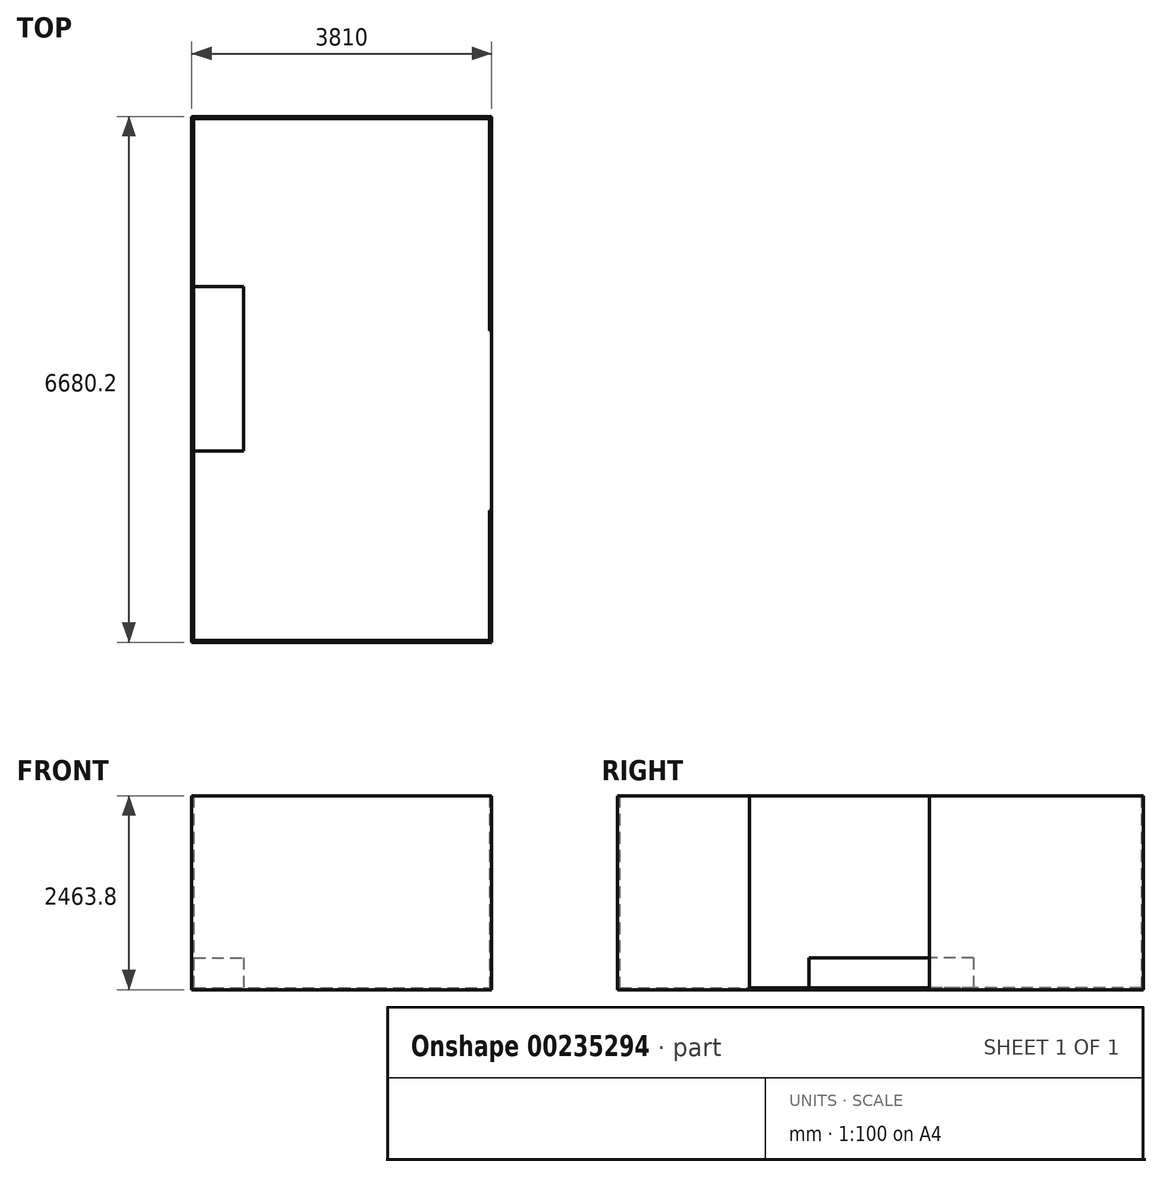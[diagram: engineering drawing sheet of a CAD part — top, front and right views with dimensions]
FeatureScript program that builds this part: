
annotation { "Feature Type Name" : "Feature", "Feature Type Description" : "" }
export const myFeature = defineFeature(function(context is Context, id is Id, definition is map)
    precondition{}
    {
        {
            var Q0;
            Q0=qCreatedBy(makeId("Top.planeOp"),FACE);
            var sketch = newSketch(context, id + "F0", { "sketchPlane" : qUnion([Q0])});
            skLineSegment(sketch, "E0", {"start": v(-1905, 3340.1) * mm, "end": v(1905, 3340.1) * mm});
            skLineSegment(sketch, "E1", {"start": v(1905, 3340.1) * mm, "end": v(1905, 622.3) * mm});
            skLineSegment(sketch, "E2", {"start": v(-1905, 3340.1) * mm, "end": v(-1905, -3340.1) * mm});
            skLineSegment(sketch, "E3", {"start": v(-1905, -3340.1) * mm, "end": v(1905, -3340.1) * mm});
            skLineSegment(sketch, "E4", {"start": v(1905, -3340.1) * mm, "end": v(1905, -1663.7) * mm});
            skLineSegment(sketch, "E5", {"start": v(0, 3340.1) * mm, "end": v(0, -3340.1) * mm, "construction": true});
            skLineSegment(sketch, "E6.0", {"start": v(1879.6, 3314.7) * mm, "end": v(1879.6, 622.3) * mm});
            skLineSegment(sketch, "E6.1", {"start": v(1879.6, -3314.7) * mm, "end": v(1879.6, -1663.7) * mm});
            skLineSegment(sketch, "E6.2", {"start": v(-1879.6, -3314.7) * mm, "end": v(1879.6, -3314.7) * mm});
            skLineSegment(sketch, "E6.3", {"start": v(-1879.6, 3314.7) * mm, "end": v(-1879.6, -3314.7) * mm});
            skLineSegment(sketch, "E6.4", {"start": v(-1879.6, 3314.7) * mm, "end": v(1879.6, 3314.7) * mm});
            skLineSegment(sketch, "E7", {"start": v(1879.6, -1663.7) * mm, "end": v(1905, -1663.7) * mm});
            skLineSegment(sketch, "E8", {"start": v(1879.6, 622.3) * mm, "end": v(1905, 622.3) * mm});
            skSolve(sketch);
        }
        {
            var Q0;
            Q0 = qSketchRegion(id + "F0", true);
            extrude(context, id + "F1", {"entities" : qUnion([Q0]), "depth" : 2438.4 * mm});
        }
        {
            var Q0;
            Q0=makeQuery(id+"F1.opExtrude","CAP_FACE",FACE,{"disambiguationData":[OSD([sQuery(id+"F0.wireOp",EDGE,"E0"),sQuery(id+"F0.wireOp",EDGE,"E1"),sQuery(id+"F0.wireOp",EDGE,"E2"),sQuery(id+"F0.wireOp",EDGE,"E3"),sQuery(id+"F0.wireOp",EDGE,"E4"),sQuery(id+"F0.wireOp",EDGE,"E6.0"),sQuery(id+"F0.wireOp",EDGE,"E6.1"),sQuery(id+"F0.wireOp",EDGE,"E6.2"),sQuery(id+"F0.wireOp",EDGE,"E6.3"),sQuery(id+"F0.wireOp",EDGE,"E6.4"),sQuery(id+"F0.wireOp",EDGE,"E7"),sQuery(id+"F0.wireOp",EDGE,"E8")])],"isStart":true});
            var sketch = newSketch(context, id + "F2", { "sketchPlane" : qUnion([Q0])});
            skLineSegment(sketch, "E9.bottom", {"start": v(-1905, 3340.1) * mm, "end": v(1905, 3340.1) * mm});
            skLineSegment(sketch, "E9.top", {"start": v(-1905, -3340.1) * mm, "end": v(1905, -3340.1) * mm});
            skLineSegment(sketch, "E9.left", {"start": v(-1905, 3340.1) * mm, "end": v(-1905, -3340.1) * mm});
            skLineSegment(sketch, "E9.right", {"start": v(1905, 3340.1) * mm, "end": v(1905, -3340.1) * mm});
            skSolve(sketch);
        }
        {
            var Q0;
            Q0 = qSketchRegion(id + "F2", true);
            extrude(context, id + "F3", {"entities" : qUnion([Q0]), "operationType" : NewBodyOperationType.ADD, "depth" : 25.4 * mm});
        }
        {
            var Q0;
            Q0=makeQuery(id+"F3.opExtrude","CAP_FACE",FACE,{"disambiguationData":[OSD([sQuery(id+"F2.wireOp",EDGE,"E9.bottom"),sQuery(id+"F2.wireOp",EDGE,"E9.top"),sQuery(id+"F2.wireOp",EDGE,"E9.left"),sQuery(id+"F2.wireOp",EDGE,"E9.right")])],"isStart":true});
            var sketch = newSketch(context, id + "F4", { "sketchPlane" : qUnion([Q0])});
            skLineSegment(sketch, "E10.bottom", {"start": v(-1879.6, 1181.1) * mm, "end": v(-1244.6, 1181.1) * mm});
            skLineSegment(sketch, "E10.top", {"start": v(-1879.6, -908.05) * mm, "end": v(-1244.6, -908.05) * mm});
            skLineSegment(sketch, "E10.left", {"start": v(-1879.6, 1181.1) * mm, "end": v(-1879.6, -908.05) * mm});
            skLineSegment(sketch, "E10.right", {"start": v(-1244.6, 1181.1) * mm, "end": v(-1244.6, -908.05) * mm});
            skSolve(sketch);
        }
        {
            var Q0;
            Q0 = qSketchRegion(id + "F4", true);
            extrude(context, id + "F5", {"entities" : qUnion([Q0]), "operationType" : NewBodyOperationType.ADD, "depth" : 381 * mm});
        }
    });
